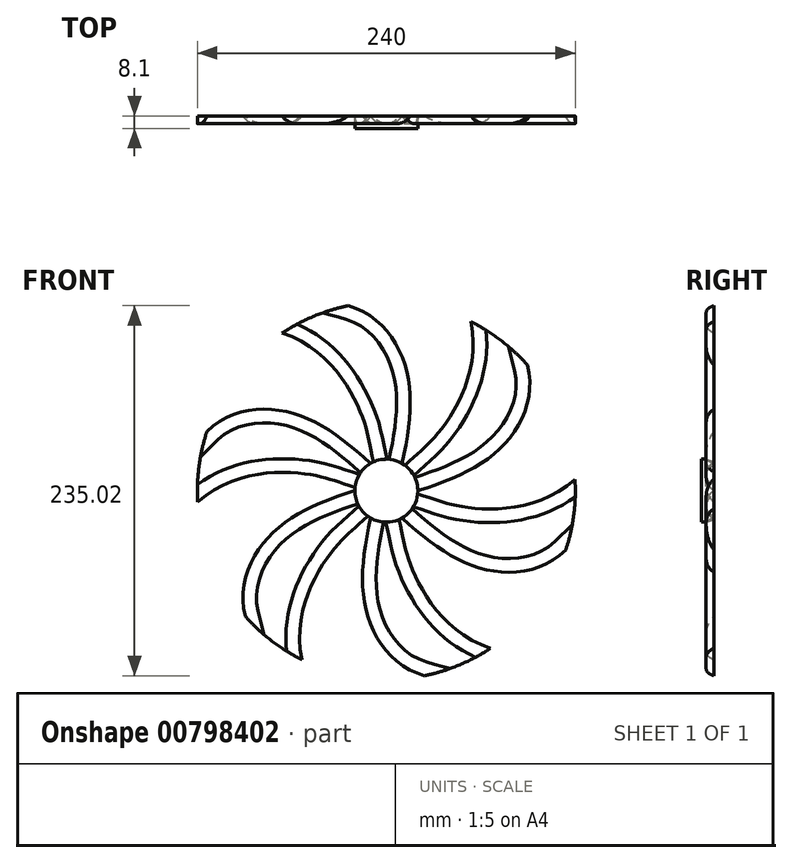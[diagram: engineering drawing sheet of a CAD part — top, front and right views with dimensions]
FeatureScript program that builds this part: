
annotation { "Feature Type Name" : "Feature", "Feature Type Description" : "" }
export const myFeature = defineFeature(function(context is Context, id is Id, definition is map)
    precondition{}
    {
        {
            var Q0;
            Q0=qCreatedBy(makeId("Front.planeOp"),FACE);
            var sketch = newSketch(context, id + "F0", { "sketchPlane" : qUnion([Q0])});
            skArc(sketch, "E0", {"start": v(89.61, 79.81) * mm, "mid": v(72.95, 95.28) * mm, "end": v(53.66, 107.33) * mm});
            skArc(sketch, "E1", {"start": v(20, 0) * mm, "mid": v(17.84, 9.05) * mm, "end": v(11.81, 16.14) * mm});
            skFitSpline(sketch, "E2", {"points": [v(11.81, 16.14) * mm, v(32.35, 35.95) * mm, v(53.66, 107.33) * mm], "startDerivative": vector(69.62, 66.54) * mm, "endDerivative": vector(-31.52, 151.14) * mm});
            skFitSpline(sketch, "E3", {"points": [v(20, 0) * mm, v(75.5, 30.2) * mm, v(89.61, 79.81) * mm], "startDerivative": vector(134.78, 42.32) * mm, "endDerivative": vector(-30.43, 118.33) * mm});
            skSolve(sketch);
        }
        {
            var Q0;
            Q0 = qSketchRegion(id + "F0", true);
            extrude(context, id + "F1", {"entities" : qUnion([Q0]), "depth" : 5 * mm, "offsetDistance" : 25 * mm});
        }
        {
            var Q0;
            Q0=makeQuery(id+"F1.opExtrude","SWEPT_BODY",BODY,{"disambiguationData":[OSD([sQuery(id+"F0.wireOp",EDGE,"E1"),sQuery(id+"F0.wireOp",EDGE,"E2"),sQuery(id+"F0.wireOp",EDGE,"E3"),sQuery(id+"F0.wireOp",EDGE,"E0")])]});
            var Q1;
            Q1=makeQuery(id+"F1.opExtrude","SWEPT_FACE",FACE,{"disambiguationData":[OSD([sQuery(id+"F0.wireOp",EDGE,"E1")])]});
            circularPattern(context, id + "F2", {"entities" : qUnion([Q0]), "axis" : qUnion([Q1]), "angle" : 360 * degree, "instanceCount" : 6, "equalSpace" : true});
        }
        {
            var Q0;
            Q0=qCreatedBy(makeId("Front.planeOp"),FACE);
            var sketch = newSketch(context, id + "F3", { "sketchPlane" : qUnion([Q0])});
            skCircle(sketch, "E4", {"center": v(0, 0) * mm, "radius": 20 * mm});
            skSolve(sketch);
        }
        {
            var Q0;
            Q0 = qSketchRegion(id + "F3", true);
            extrude(context, id + "F4", {"entities" : qUnion([Q0]), "operationType" : NewBodyOperationType.ADD, "depth" : 8.1 * mm, "offsetDistance" : 25 * mm});
        }
        {
            var Q0;
            Q0=makeQuery(id+"F2.opPattern","COPY",EDGE,{"derivedFrom":makeQuery(id+"F1.opExtrude","CAP_EDGE",EDGE,{"disambiguationData":[OSD([sQuery(id+"F0.wireOp",EDGE,"E2")])],"isStart":false}),"instanceName":"1"});
            var Q1;
            Q1=makeQuery(id+"F2.opPattern","COPY",EDGE,{"derivedFrom":makeQuery(id+"F1.opExtrude","CAP_EDGE",EDGE,{"disambiguationData":[OSD([sQuery(id+"F0.wireOp",EDGE,"E3")])],"isStart":false}),"instanceName":"1"});
            var Q2;
            Q2=makeQuery(id+"F1.opExtrude","CAP_EDGE",EDGE,{"disambiguationData":[OSD([sQuery(id+"F0.wireOp",EDGE,"E2")])],"isStart":false});
            var Q3;
            Q3=makeQuery(id+"F1.opExtrude","CAP_EDGE",EDGE,{"disambiguationData":[OSD([sQuery(id+"F0.wireOp",EDGE,"E3")])],"isStart":false});
            var Q4;
            Q4=makeQuery(id+"F2.opPattern","COPY",EDGE,{"derivedFrom":makeQuery(id+"F1.opExtrude","CAP_EDGE",EDGE,{"disambiguationData":[OSD([sQuery(id+"F0.wireOp",EDGE,"E2")])],"isStart":false}),"instanceName":"5"});
            var Q5;
            Q5=makeQuery(id+"F2.opPattern","COPY",EDGE,{"derivedFrom":makeQuery(id+"F1.opExtrude","CAP_EDGE",EDGE,{"disambiguationData":[OSD([sQuery(id+"F0.wireOp",EDGE,"E3")])],"isStart":false}),"instanceName":"5"});
            var Q6;
            Q6=makeQuery(id+"F2.opPattern","COPY",EDGE,{"derivedFrom":makeQuery(id+"F1.opExtrude","CAP_EDGE",EDGE,{"disambiguationData":[OSD([sQuery(id+"F0.wireOp",EDGE,"E2")])],"isStart":false}),"instanceName":"4"});
            var Q7;
            Q7=makeQuery(id+"F2.opPattern","COPY",EDGE,{"derivedFrom":makeQuery(id+"F1.opExtrude","CAP_EDGE",EDGE,{"disambiguationData":[OSD([sQuery(id+"F0.wireOp",EDGE,"E3")])],"isStart":false}),"instanceName":"4"});
            var Q8;
            Q8=makeQuery(id+"F2.opPattern","COPY",EDGE,{"derivedFrom":makeQuery(id+"F1.opExtrude","CAP_EDGE",EDGE,{"disambiguationData":[OSD([sQuery(id+"F0.wireOp",EDGE,"E2")])],"isStart":false}),"instanceName":"3"});
            var Q9;
            Q9=makeQuery(id+"F2.opPattern","COPY",EDGE,{"derivedFrom":makeQuery(id+"F1.opExtrude","CAP_EDGE",EDGE,{"disambiguationData":[OSD([sQuery(id+"F0.wireOp",EDGE,"E2")])],"isStart":false}),"instanceName":"2"});
            var Q10;
            Q10=makeQuery(id+"F2.opPattern","COPY",EDGE,{"derivedFrom":makeQuery(id+"F1.opExtrude","CAP_EDGE",EDGE,{"disambiguationData":[OSD([sQuery(id+"F0.wireOp",EDGE,"E3")])],"isStart":false}),"instanceName":"2"});
            var Q11;
            Q11=makeQuery(id+"F2.opPattern","COPY",EDGE,{"derivedFrom":makeQuery(id+"F1.opExtrude","CAP_EDGE",EDGE,{"disambiguationData":[OSD([sQuery(id+"F0.wireOp",EDGE,"E3")])],"isStart":false}),"instanceName":"3"});
            fillet(context, id + "F5", {"entities" : qUnion([Q0, Q1, Q2, Q3, Q4, Q5, Q6, Q7, Q8, Q9, Q10, Q11]), "radius" : 10 * mm, "tangentPropagation" : true, "allowEdgeOverflow" : false});
        }
    });
